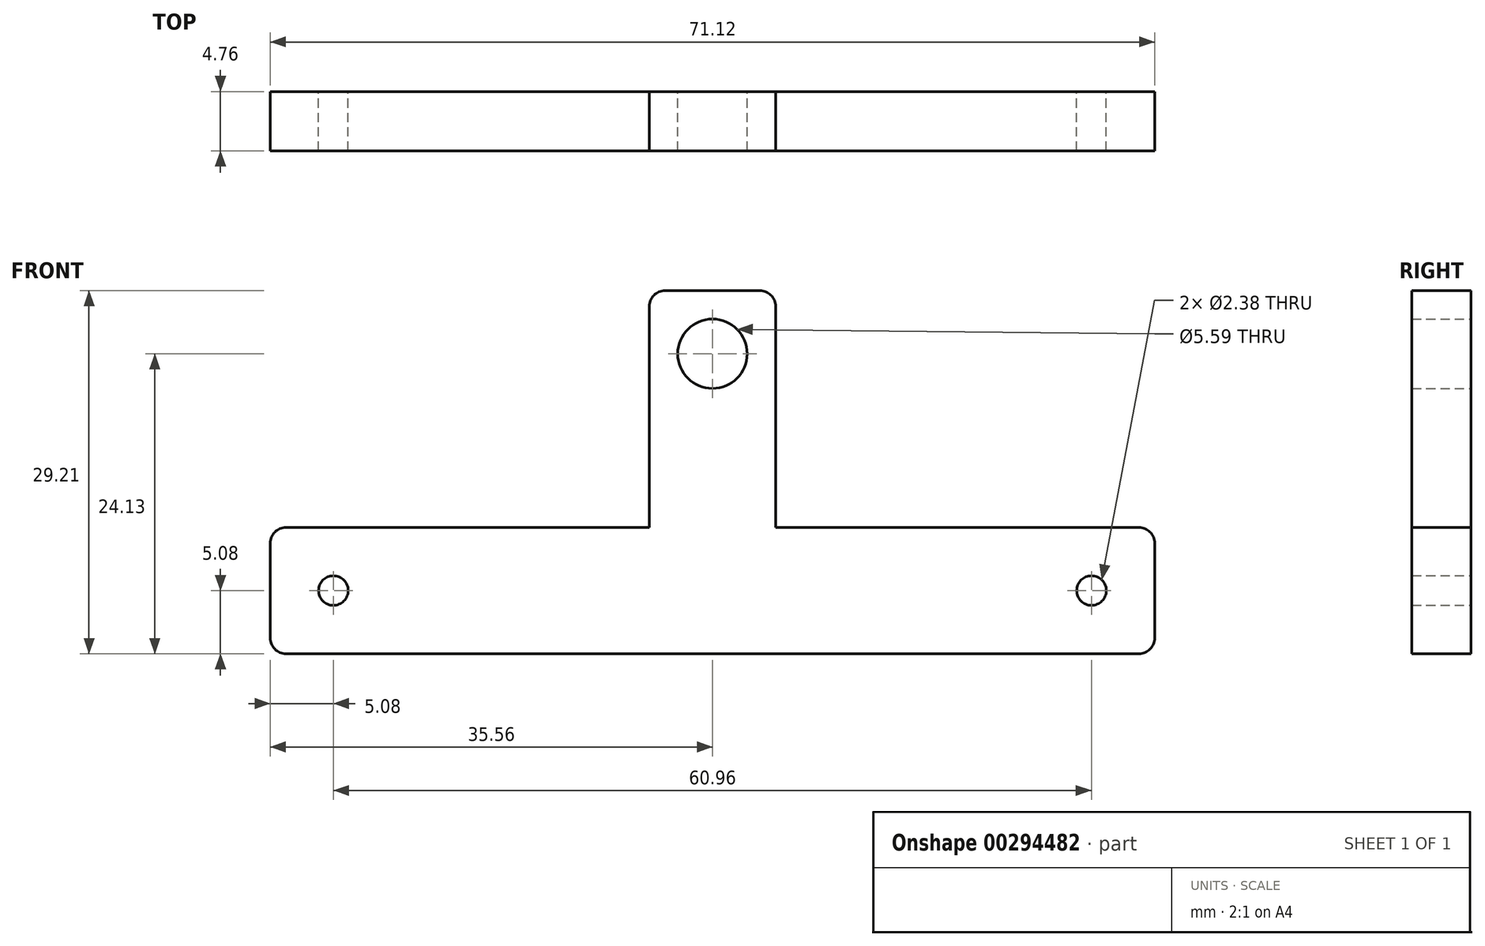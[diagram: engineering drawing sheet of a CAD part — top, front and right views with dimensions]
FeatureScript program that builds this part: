
annotation { "Feature Type Name" : "Feature", "Feature Type Description" : "" }
export const myFeature = defineFeature(function(context is Context, id is Id, definition is map)
    precondition{}
    {
        {
            var Q0;
            Q0=qCreatedBy(makeId("Front.planeOp"),FACE);
            var sketch = newSketch(context, id + "F0", { "sketchPlane" : qUnion([Q0])});
            skLineSegment(sketch, "E0.bottom", {"start": v(35.56, 5.08) * mm, "end": v(-35.56, 5.08) * mm});
            skLineSegment(sketch, "E0.top", {"start": v(35.56, -5.08) * mm, "end": v(-35.56, -5.08) * mm});
            skLineSegment(sketch, "E0.left", {"start": v(35.56, 5.08) * mm, "end": v(35.56, -5.08) * mm});
            skLineSegment(sketch, "E0.right", {"start": v(-35.56, 5.08) * mm, "end": v(-35.56, -5.08) * mm});
            skPoint(sketch, "E0.middle", {"position": v(0, 0) * mm});
            skLineSegment(sketch, "E1", {"start": v(0, 0) * mm, "end": v(0, 24.13) * mm});
            skLineSegment(sketch, "E2.bottom", {"start": v(-5.08, 24.13) * mm, "end": v(5.08, 24.13) * mm});
            skLineSegment(sketch, "E2.top", {"start": v(-5.08, 5.08) * mm, "end": v(5.08, 5.08) * mm});
            skLineSegment(sketch, "E2.left", {"start": v(-5.08, 24.13) * mm, "end": v(-5.08, 5.08) * mm});
            skLineSegment(sketch, "E2.right", {"start": v(5.08, 24.13) * mm, "end": v(5.08, 5.08) * mm});
            skCircle(sketch, "E3", {"center": v(0, 19.05) * mm, "radius": 2.8 * mm});
            skCircle(sketch, "E4", {"center": v(30.48, 0) * mm, "radius": 1.2 * mm});
            skCircle(sketch, "E5", {"center": v(-30.48, 0) * mm, "radius": 1.2 * mm});
            skPoint(sketch, "E6.oppositeSnap0", {"position": v(35.56, 0) * mm});
            skLineSegment(sketch, "E6.left", {"start": v(5.08, 14.6) * mm, "end": v(5.08, 24.13) * mm});
            skCircle(sketch, "E7", {"center": v(30.48, 19.37) * mm, "radius": 1.2 * mm});
            skPoint(sketch, "E7.centerSnap0", {"position": v(5.08, 19.37) * mm});
            skSolve(sketch);
        }
        {
            var Q0;
            {var subQ0=sQuery(id+"F0.wireOp",EDGE,"E2.right");Q0=makeQuery(id+"F0.imprint","IMPRINT",FACE,{"disambiguationData":[TD([[makeQuery(id+"F0.imprint","IMPRINT",EDGE,{"derivedFrom":subQ0}),-1.0]])]});}
            var Q1;
            {var subQ3=sQuery(id+"F0.wireOp",EDGE,"E2.left");Q1=makeQuery(id+"F0.imprint","IMPRINT",FACE,{"disambiguationData":[TD([[makeQuery(id+"F0.imprint","IMPRINT",EDGE,{"derivedFrom":subQ3}),1.0]])]});}
            var Q2;
            Q2=makeQuery(id+"F0.imprint","IMPRINT",FACE,{"disambiguationData":[TD([[makeQuery(id+"F0.imprint","IMPRINT",EDGE,{"derivedFrom":sQuery(id+"F0.wireOp",EDGE,"E0.top")}),-1.0]])]});
            var Q3;
            Q3=makeQuery(id+"F0.imprint","IMPRINT",FACE,{"disambiguationData":[TD([[makeQuery(id+"F0.imprint","IMPRINT",EDGE,{"derivedFrom":sQuery(id+"F0.wireOp",EDGE,"E6.bottom")}),1.0]])]});
            extrude(context, id + "F1", {"entities" : qUnion([Q0, Q1, Q2, Q3]), "depth" : 4.76 * mm});
        }
        {
            var Q0;
            Q0=makeQuery(id+"F1.opExtrude","SWEPT_EDGE",EDGE,{"disambiguationData":[OSD([sQuery(id+"F0.wireOp",EDGE,"E2.bottom"),sQuery(id+"F0.wireOp",EDGE,"E2.left")])]});
            var Q1;
            Q1=makeQuery(id+"F1.opExtrude","SWEPT_EDGE",EDGE,{"disambiguationData":[OSD([sQuery(id+"F0.wireOp",EDGE,"E2.bottom"),sQuery(id+"F0.wireOp",EDGE,"E2.right")])]});
            var Q2;
            Q2=makeQuery(id+"F1.opExtrude","SWEPT_EDGE",EDGE,{"disambiguationData":[OSD([sQuery(id+"F0.wireOp",EDGE,"E0.bottom"),sQuery(id+"F0.wireOp",EDGE,"E0.left")])]});
            var Q3;
            Q3=makeQuery(id+"F1.opExtrude","SWEPT_EDGE",EDGE,{"disambiguationData":[OSD([sQuery(id+"F0.wireOp",EDGE,"E0.top"),sQuery(id+"F0.wireOp",EDGE,"E0.left")])]});
            var Q4;
            Q4=makeQuery(id+"F1.opExtrude","SWEPT_EDGE",EDGE,{"disambiguationData":[OSD([sQuery(id+"F0.wireOp",EDGE,"E0.top"),sQuery(id+"F0.wireOp",EDGE,"E0.right")])]});
            var Q5;
            Q5=makeQuery(id+"F1.opExtrude","SWEPT_EDGE",EDGE,{"disambiguationData":[OSD([sQuery(id+"F0.wireOp",EDGE,"E0.bottom"),sQuery(id+"F0.wireOp",EDGE,"E0.right")])]});
            fillet(context, id + "F2", {"entities" : qUnion([Q0, Q1, Q2, Q3, Q4, Q5]), "radius" : 1.27 * mm, "tangentPropagation" : true, "allowEdgeOverflow" : false});
        }
    });
